# Revit family: Haworth_EmbroiderySimple_Lounge_Chair
name_source: partatom
category: Furniture
revit_build: Autodesk Revit 2018 (Build: 20170223_1515(x64)
units: mm (PartAtom-declared; Revit-internal decimal feet)

## family parameters
Always vertical = Yes
Cut with Voids When Loaded = No
OmniClass Number = 23.40.20.00
OmniClass Title = General Furniture and Specialties
Room Calculation Point = No
Shared = No
Work Plane-Based = No

## types (1)
- HCCE-EML1
    Actual Depth = 2' - 0 1/4"
    Actual Height = 2' - 7 1/2"
    Actual Width = 2' - 8 1/2"
    Assembly Code = E2020200
    Base Finish = Haworth _ Paint _ Collection Anthracite
    Description = Haworth Embroidery Simple Lounge Chair
    Glide Finish = Haworth _ Polymer _ Slate
    Manufacturer = Haworth
    Model = HCCE-EML1
    Revision = 1
    Seat Height = 1' - 2 3/4"
    Size = Verify Final Dim. w/ Haworth
    URL = http://www.haworth.com
    URL - Product = https://www.haworth.com
    Warranty = http://www.haworth.com

## geometry (parser evidence)
native form markers: Sweep x2
no freeform markers — native parametric forms only
